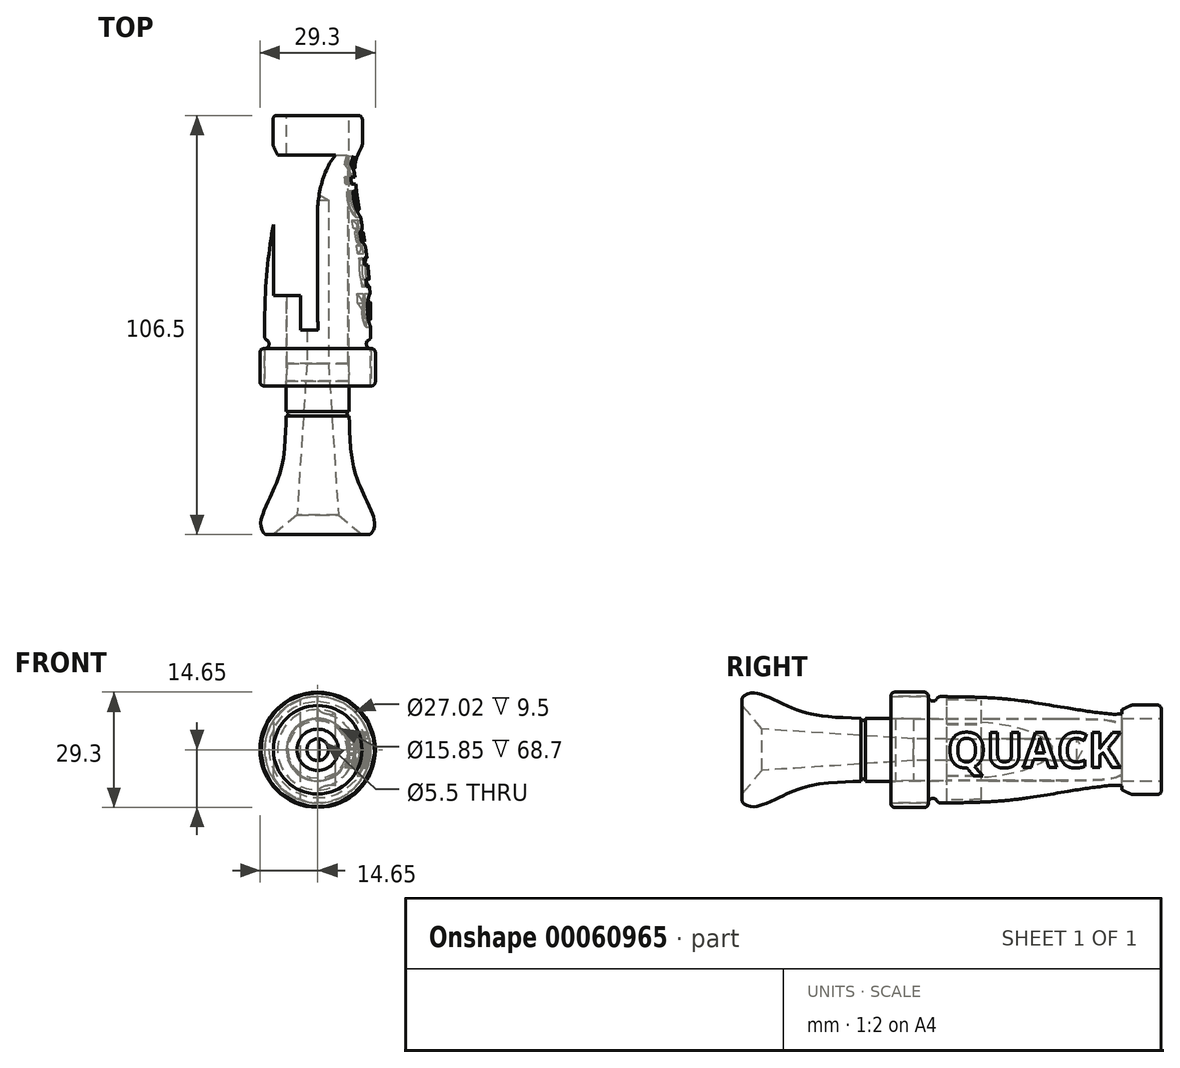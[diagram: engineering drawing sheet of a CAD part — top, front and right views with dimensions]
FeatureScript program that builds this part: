
annotation { "Feature Type Name" : "Feature", "Feature Type Description" : "" }
export const myFeature = defineFeature(function(context is Context, id is Id, definition is map)
    precondition{}
    {
        {
            var Q0;
            Q0=qCreatedBy(makeId("Top.planeOp"),FACE);
            var sketch = newSketch(context, id + "F0", { "sketchPlane" : qUnion([Q0])});
            skLineSegment(sketch, "E0", {"start": v(0, 34.01) * mm, "end": v(0, -44.14) * mm, "construction": true});
            skLineSegment(sketch, "E1", {"start": v(0, 28.73) * mm, "end": v(11.35, 28.73) * mm});
            skLineSegment(sketch, "E2", {"start": v(11.35, 28.73) * mm, "end": v(11.35, 21.23) * mm});
            skFitSpline(sketch, "E3", {"points": [v(11.35, 21.23) * mm, v(9.5, 16.23) * mm, v(12.1, -4.33) * mm, v(13.5, -28.17) * mm], "startDerivative": vector(-11.43, -29.25) * mm, "endDerivative": vector(0.17, -68.71) * mm});
            skLineSegment(sketch, "E4", {"start": v(0, -39.97) * mm, "end": v(0, 28.73) * mm});
            skArc(sketch, "E5", {"start": v(13.5, -28.17) * mm, "mid": v(12.35, -29.32) * mm, "end": v(13.5, -30.47) * mm});
            skLineSegment(sketch, "E6", {"start": v(13.5, -30.47) * mm, "end": v(13.5, -39.97) * mm});
            skLineSegment(sketch, "E7", {"start": v(13.5, -39.97) * mm, "end": v(0, -39.97) * mm});
            skSolve(sketch);
        }
        {
            var Q0;
            Q0=makeQuery(id+"F0.imprint","IMPRINT",FACE,{"disambiguationData":[TD([[makeQuery(id+"F0.imprint","IMPRINT",EDGE,{"derivedFrom":sQuery(id+"F0.wireOp",EDGE,"E1")}),-1.0]])]});
            var Q1;
            Q1=sQuery(id+"F0.wireOp",EDGE,"E0");
            revolve(context, id + "F1", {"entities" : qUnion([Q0]), "axis" : qUnion([Q1]), "revolveType" : RevolveType.FULL});
        }
        {
            var Q0;
            Q0=makeQuery(id+"F1.opRevolve","SWEPT_FACE",FACE,{"disambiguationData":[OSD([sQuery(id+"F0.wireOp",EDGE,"E1")])]});
            var sketch = newSketch(context, id + "F2", { "sketchPlane" : qUnion([Q0])});
            skCircle(sketch, "E8", {"center": v(0, 0) * mm, "radius": 7.92 * mm});
            skSolve(sketch);
        }
        {
            var Q0;
            Q0=makeQuery(id+"F2.imprint","IMPRINT",FACE,{"disambiguationData":[TD([[makeQuery(id+"F2.imprint","IMPRINT",EDGE,{"derivedFrom":sQuery(id+"F2.wireOp",EDGE,"E8")}),1.0]])]});
            extrude(context, id + "F3", {"entities" : qUnion([Q0]), "operationType" : NewBodyOperationType.REMOVE, "endBound" : BoundingType.THROUGH_ALL, "oppositeDirection" : true, "depth" : 25 * mm});
        }
        {
            var Q0;
            Q0=makeQuery(id+"F1.opRevolve","SWEPT_EDGE",EDGE,{"disambiguationData":[OSD([sQuery(id+"F0.wireOp",EDGE,"E1"),sQuery(id+"F0.wireOp",EDGE,"E2")])]});
            var Q1;
            Q1=makeQuery(id+"F1.opRevolve","SWEPT_EDGE",EDGE,{"disambiguationData":[OSD([sQuery(id+"F0.wireOp",EDGE,"E2"),sQuery(id+"F0.wireOp",EDGE,"E3")])]});
            var Q2;
            Q2=makeQuery(id+"F1.opRevolve","SWEPT_EDGE",EDGE,{"disambiguationData":[OSD([sQuery(id+"F0.wireOp",EDGE,"E3"),sQuery(id+"F0.wireOp",EDGE,"E5")])]});
            var Q3;
            Q3=makeQuery(id+"F1.opRevolve","SWEPT_EDGE",EDGE,{"disambiguationData":[OSD([sQuery(id+"F0.wireOp",EDGE,"E5"),sQuery(id+"F0.wireOp",EDGE,"E6")])]});
            var Q4;
            Q4=makeQuery(id+"F3.boolean.opBoolean","COPY",EDGE,{"derivedFrom":makeQuery(id+"F3.opExtrude","CAP_EDGE",EDGE,{"disambiguationData":[OSD([sQuery(id+"F2.wireOp",EDGE,"E8")])],"isStart":true})});
            fillet(context, id + "F4", {"entities" : qUnion([Q0, Q1, Q2, Q3, Q4]), "radius" : 1 * mm, "tangentPropagation" : true, "allowEdgeOverflow" : false});
        }
        {
            var Q0;
            Q0=qCreatedBy(makeId("Top.planeOp"),FACE);
            var sketch = newSketch(context, id + "F5", { "sketchPlane" : qUnion([Q0])});
            skLineSegment(sketch, "E9", {"start": v(0, 28.63) * mm, "end": v(0, -88.47) * mm, "construction": true});
            skLineSegment(sketch, "E10", {"start": v(0, 18.73) * mm, "end": v(7.78, 18.73) * mm});
            skLineSegment(sketch, "E11", {"start": v(0, -77.77) * mm, "end": v(13.38, -77.77) * mm});
            skLineSegment(sketch, "E12", {"start": v(7.78, 18.73) * mm, "end": v(7.78, -34.27) * mm});
            skFitSpline(sketch, "E13", {"points": [v(13.38, -77.77) * mm, v(14.03, -72.8) * mm, v(10.25, -64.12) * mm, v(8, -47.6) * mm], "startDerivative": vector(17.39, 21.88) * mm, "endDerivative": vector(-1.44, 59.8) * mm});
            skLineSegment(sketch, "E14", {"start": v(-21.94, -39.77) * mm, "end": v(21.19, -39.77) * mm, "construction": true});
            skArc(sketch, "E15", {"start": v(8, -46.45) * mm, "mid": v(7.43, -47.02) * mm, "end": v(8, -47.6) * mm});
            skLineSegment(sketch, "E16", {"start": v(7.78, -34.27) * mm, "end": v(8, -38.77) * mm});
            skLineSegment(sketch, "E17", {"start": v(8, -38.77) * mm, "end": v(8, -46.45) * mm});
            skLineSegment(sketch, "E18", {"start": v(0, 18.73) * mm, "end": v(0, -77.77) * mm});
            skPoint(sketch, "E19", {"position": v(0, -77.77) * mm});
            skSolve(sketch);
        }
        {
            var Q0;
            Q0 = qSketchRegion(id + "F5", true);
            var Q1;
            Q1=sQuery(id+"F5.wireOp",EDGE,"E18");
            revolve(context, id + "F6", {"entities" : qUnion([Q0]), "axis" : qUnion([Q1]), "revolveType" : RevolveType.FULL});
        }
        {
            var Q0;
            Q0=makeQuery(id+"F6.opRevolve","SWEPT_FACE",FACE,{"disambiguationData":[OSD([sQuery(id+"F5.wireOp",EDGE,"E11")])]});
            var sketch = newSketch(context, id + "F7", { "sketchPlane" : qUnion([Q0])});
            skPoint(sketch, "E20", {"position": v(0, 0) * mm});
            skSolve(sketch);
        }
        {
            var Q0;
            Q0=sQuery(id+"F7.wireOp",VERTEX,"E20");
            var Q1;
            Q1=makeQuery(id+"F6.opRevolve","SWEPT_BODY",BODY,{"disambiguationData":[OSD([sQuery(id+"F5.wireOp",EDGE,"E10"),sQuery(id+"F5.wireOp",EDGE,"E11"),sQuery(id+"F5.wireOp",EDGE,"E12"),sQuery(id+"F5.wireOp",EDGE,"E13"),sQuery(id+"F5.wireOp",EDGE,"E15"),sQuery(id+"F5.wireOp",EDGE,"E16"),sQuery(id+"F5.wireOp",EDGE,"E17"),sQuery(id+"F5.wireOp",EDGE,"E18")])]});
            hole(context, id + "F8", {"style" : HoleStyle.SIMPLE, "holeDiameter" : 5.5 * mm, "endStyle" : HoleEndStyle.BLIND, "holeDepth" : 85 * mm, "locations" : qUnion([Q0]), "scope" : qUnion([Q1])});
        }
        {
            var Q0;
            Q0=qCreatedBy(makeId("Top.planeOp"),FACE);
            var sketch = newSketch(context, id + "F9", { "sketchPlane" : qUnion([Q0])});
            skLineSegment(sketch, "E21", {"start": v(0, 26.5) * mm, "end": v(0, -88.94) * mm, "construction": true});
            skLineSegment(sketch, "E22.0", {"start": v(0, -77.77) * mm, "end": v(11.25, -77.77) * mm});
            skLineSegment(sketch, "E23", {"start": v(11.25, -77.77) * mm, "end": v(5.25, -72.77) * mm});
            skLineSegment(sketch, "E24", {"start": v(5.25, -72.77) * mm, "end": v(2.75, -34.27) * mm});
            skLineSegment(sketch, "E25", {"start": v(2.75, -34.27) * mm, "end": v(0, -34.27) * mm});
            skLineSegment(sketch, "E26", {"start": v(0, -34.27) * mm, "end": v(0, -77.77) * mm});
            skPoint(sketch, "E27.orphan", {"position": v(-13.37, -77.77) * mm});
            skPoint(sketch, "E28.orphan", {"position": v(13.38, -77.77) * mm});
            skSolve(sketch);
        }
        {
            var Q0;
            Q0 = qSketchRegion(id + "F9", true);
            var Q1;
            Q1=sQuery(id+"F9.wireOp",EDGE,"E26");
            revolve(context, id + "F10", {"operationType" : NewBodyOperationType.REMOVE, "entities" : qUnion([Q0]), "axis" : qUnion([Q1]), "revolveType" : RevolveType.FULL, "oppositeDirection" : true});
        }
        {
            var Q0;
            Q0=makeQuery(id+"F10.boolean.opBoolean","COPY",EDGE,{"derivedFrom":makeQuery(id+"F10.opRevolve","SWEPT_EDGE",EDGE,{"disambiguationData":[OSD([sQuery(id+"F9.wireOp",EDGE,"E22.0"),sQuery(id+"F9.wireOp",EDGE,"E23")])]})});
            var Q1;
            Q1=makeQuery(id+"F6.opRevolve","SWEPT_EDGE",EDGE,{"disambiguationData":[OSD([sQuery(id+"F5.wireOp",EDGE,"E11"),sQuery(id+"F5.wireOp",EDGE,"E13")])]});
            fillet(context, id + "F11", {"entities" : qUnion([Q0, Q1]), "radius" : 1 * mm, "tangentPropagation" : true, "allowEdgeOverflow" : false});
        }
        {
            var Q0;
            Q0=qCreatedBy(makeId("Top.planeOp"),FACE);
            var sketch = newSketch(context, id + "F12", { "sketchPlane" : qUnion([Q0])});
            skLineSegment(sketch, "E29", {"start": v(0.05, -25.77) * mm, "end": v(-4.3, -25.77) * mm});
            skLineSegment(sketch, "E30", {"start": v(-4.3, -25.77) * mm, "end": v(-4.3, -17.02) * mm});
            skLineSegment(sketch, "E31", {"start": v(-4.3, -17.02) * mm, "end": v(-11.23, -17.02) * mm});
            skLineSegment(sketch, "E32", {"start": v(-11.23, -17.02) * mm, "end": v(-11.23, 18.73) * mm});
            skLineSegment(sketch, "E33.0", {"start": v(-7.78, 18.73) * mm, "end": v(4.53, 18.73) * mm});
            skFitSpline(sketch, "E34", {"points": [v(-0.08, 0.73) * mm, v(4.53, 18.73) * mm], "startDerivative": vector(-0.06, 12.7) * mm, "endDerivative": vector(14.01, 17.84) * mm});
            skPoint(sketch, "E35.orphan", {"position": v(7.78, 18.73) * mm});
            skLineSegment(sketch, "E36.trimOffspring", {"start": v(-0.08, 0.73) * mm, "end": v(0.05, -25.77) * mm});
            skLineSegment(sketch, "E37", {"start": v(4.53, 18.73) * mm, "end": v(-11.23, 18.73) * mm});
            skSolve(sketch);
        }
        {
            var Q0;
            Q0=makeQuery(id+"F12.imprint","IMPRINT",FACE,{"disambiguationData":[TD([[makeQuery(id+"F12.imprint","IMPRINT",EDGE,{"derivedFrom":sQuery(id+"F12.wireOp",EDGE,"E29")}),-1.0]])]});
            extrude(context, id + "F13", {"entities" : qUnion([Q0]), "operationType" : NewBodyOperationType.REMOVE, "endBound" : BoundingType.THROUGH_ALL, "oppositeDirection" : true, "depth" : 25 * mm, "hasSecondDirection" : true, "secondDirectionBound" : SecondDirectionBoundingType.THROUGH_ALL, "secondDirectionOppositeDirection" : false, "secondDirectionDepth" : 25 * mm});
        }
        {
            var Q0;
            Q0=makeQuery(id+"F1.opRevolve","SWEPT_FACE",FACE,{"disambiguationData":[OSD([sQuery(id+"F0.wireOp",EDGE,"E7")])]});
            var sketch = newSketch(context, id + "F14", { "sketchPlane" : qUnion([Q0])});
            skCircle(sketch, "E38.0", {"center": v(0, 0) * mm, "radius": 13.51 * mm});
            skCircle(sketch, "E39", {"center": v(0, 0) * mm, "radius": 14.65 * mm});
            skSolve(sketch);
        }
        {
            var Q0;
            Q0 = qSketchRegion(id + "F14", true);
            extrude(context, id + "F15", {"entities" : qUnion([Q0]), "oppositeDirection" : true, "depth" : 9.5 * mm});
        }
        {
            var Q0;
            Q0=makeQuery(id+"F15.opExtrude","CAP_EDGE",EDGE,{"disambiguationData":[OSD([sQuery(id+"F14.wireOp",EDGE,"E39")])],"isStart":true});
            var Q1;
            Q1=makeQuery(id+"F15.opExtrude","CAP_EDGE",EDGE,{"disambiguationData":[OSD([sQuery(id+"F14.wireOp",EDGE,"E39")])],"isStart":false});
            fillet(context, id + "F16", {"entities" : qUnion([Q0, Q1]), "radius" : 1 * mm, "tangentPropagation" : true, "allowEdgeOverflow" : false});
        }
        {
            var Q0;
            Q0=qCreatedBy(makeId("Top.planeOp"),FACE);
            var sketch = newSketch(context, id + "F17", { "sketchPlane" : qUnion([Q0])});
            skLineSegment(sketch, "E40.0", {"start": v(0, 34.01) * mm, "end": v(0, -44.14) * mm});
            skLineSegment(sketch, "E40.4", {"start": v(0, -39.97) * mm, "end": v(0, 28.73) * mm});
            skLineSegment(sketch, "E41", {"start": v(10, 21.23) * mm, "end": v(0, 21.23) * mm});
            skLineSegment(sketch, "E42", {"start": v(12.25, -28.17) * mm, "end": v(0, -28.17) * mm});
            skFitSpline(sketch, "E43.0", {"points": [v(10.19, 21.68) * mm, v(9.97, 21.13) * mm, v(9.62, 20.42) * mm, v(9.15, 19.46) * mm, v(8.8, 18.66) * mm, v(8.5, 17.76) * mm, v(8.28, 16.72) * mm, v(8.18, 15.53) * mm, v(8.17, 14.22) * mm, v(8.25, 12.78) * mm, v(8.44, 10.71) * mm, v(8.82, 7.88) * mm, v(9.42, 4.22) * mm, v(9.97, 1.07) * mm, v(10.39, -1.43) * mm, v(10.69, -3.28) * mm, v(10.96, -5.07) * mm, v(11.27, -7.4) * mm, v(11.6, -10.19) * mm, v(11.87, -13.49) * mm, v(12.06, -16.82) * mm, v(12.21, -21.47) * mm, v(12.24, -25.31) * mm, v(12.25, -28.17) * mm, v(10.19, 21.68) * mm]});
            skFitSpline(sketch, "E44.0", {"points": [v(10.19, 21.68) * mm, v(9.97, 21.13) * mm, v(9.62, 20.42) * mm, v(9.15, 19.46) * mm, v(8.8, 18.66) * mm, v(8.5, 17.76) * mm, v(8.28, 16.72) * mm, v(8.18, 15.53) * mm, v(8.17, 14.22) * mm, v(8.25, 12.78) * mm, v(8.44, 10.71) * mm, v(8.82, 7.88) * mm, v(9.42, 4.22) * mm, v(9.97, 1.07) * mm, v(10.39, -1.43) * mm, v(10.69, -3.28) * mm, v(10.96, -5.07) * mm, v(11.27, -7.4) * mm, v(11.6, -10.19) * mm, v(11.87, -13.49) * mm, v(12.06, -16.82) * mm, v(12.21, -21.47) * mm, v(12.24, -25.31) * mm, v(12.25, -28.17) * mm]});
            skSolve(sketch);
        }
        {
            var Q0;
            Q0 = qSketchRegion(id + "F17", true);
            var Q1;
            Q1=sQuery(id+"F17.wireOp",EDGE,"E44.0");
            var Q2;
            Q2=sQuery(id+"F17.wireOp",EDGE,"E40.4");
            revolve(context, id + "F18", {"bodyType" : ToolBodyType.SURFACE, "entities" : qUnion([Q0]), "surfaceEntities" : qUnion([Q1]), "axis" : qUnion([Q2]), "revolveType" : RevolveType.FULL});
        }
        {
            var Q0;
            Q0=qCreatedBy(makeId("Right.planeOp"),FACE);
            cPlane(context, id + "F19", {"entities" : qUnion([Q0]), "cplaneType" : CPlaneType.OFFSET, "offset" : 15 * mm, "width" : 150 * mm, "height" : 150 * mm});
        }
        {
            var Q0;
            Q0=qCreatedBy(id+"F19.planeOp",FACE);
            var sketch = newSketch(context, id + "F20", { "sketchPlane" : qUnion([Q0])});
            skText(sketch, "E45", { "text": "QUACK", "fontName": "OpenSans-Bold.ttf"});
            const initialGuessF20  = {"E45": [-0.0257, -0.00454, 1, 0, 0.00896]};
            skSetInitialGuess(sketch, initialGuessF20);
            skSolve(sketch);
        }
        {
            var Q0;
            Q0 = qSketchRegion(id + "F20", true);
            var Q1;
            Q1=makeQuery(id+"F18.opRevolve","SWEPT_FACE",FACE,{"disambiguationData":[OSD([sQuery(id+"F17.wireOp",EDGE,"E44.0")])]});
            var Q2;
            Q2=makeQuery(id+"F18.opRevolve","SWEPT_FACE",FACE,{"disambiguationData":[OSD([sQuery(id+"F17.wireOp",EDGE,"E44.0")])]});
            extrude(context, id + "F21", {"entities" : qUnion([Q0]), "operationType" : NewBodyOperationType.REMOVE, "endBound" : BoundingType.UP_TO_SURFACE, "oppositeDirection" : true, "endBoundEntityFace" : qUnion([Q1]), "depth" : 25 * mm});
        }
    });
